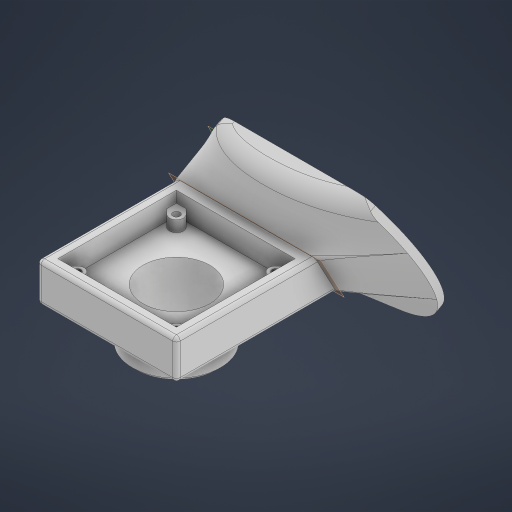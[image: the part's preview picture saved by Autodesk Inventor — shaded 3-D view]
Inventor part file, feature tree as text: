
AUTODESK INVENTOR PART (.ipt)
format: ipt  version: 2023 (Build 270158000, 158)  size: 585,216 bytes
history: native  units: in
note: dims shown in document units (in); Inventor stores cm internally (conversion verified against a paired STEP export)
features: sketch x10, extrude x7, hole x3, fillet x3, plane x2, chamfer x2, other x2, projected_geometry x2, loft x1
ambient origin geometry x8: Origin, YZ Plane, XZ Plane, XY Plane, X Axis, Y Axis, Z Axis, Center Point
bodies: Solid1 (feature_tree)
feature tree (32):
  extrude  "Extrusion1"  Depth=0.525in
  extrude  "Extrusion2"  Depth=0.4252in
  plane  "Work Plane1"
  extrude  "Extrusion3"  Depth=0.6in
  loft  "Loft1"
  extrude  "Extrusion4"  TaperAngle=0.0deg  [1 undecoded]
  hole  "Hole1"  [1 undecoded]
  extrude  "Extrusion5"  Depth=1.1875in
  extrude  "Extrusion6"  Depth=0.1839in
  hole  "Hole2"  [1 undecoded]
  plane  "Work Plane2"
  hole  "Hole3"  [1 undecoded]
  fillet  "Fillet1"  Radius=0.9792in
  chamfer  "Chamfer1"  Angle=45.0deg  [1 undecoded]
  fillet  "Fillet2"  Radius=0.3in
  extrude  "Extrusion7"  Depth=0.15in
  fillet  "Fillet3"  Radius=0.05in
  chamfer  "Chamfer2"  Distance=0.05in Angle=45.0deg
  sketch  "Sketch1"  dims[d0=1.875in d1=0.525in]
  sketch  "Sketch2"  dims[d2=1.875in d3=0.0in d4=0.4252in]
  sketch  "Sketch3"  dims[d5=1.875in d6=0.0in d7=0.6in]
  other  "Edges1"
  other  "Edges2"
  sketch  "Sketch4"  dims[d9=2.75in d10=0.1in d11=0.0in]
  projected_geometry  "Projected Loop1"
  sketch  "Sketch5"  dims[d12=0.0in d13=90.0deg d14=0.0in d15=90.0deg]
  sketch  "Sketch6"  dims[d16=1.6in d17=0.3in d18=0.0in]
  sketch  "Sketch7"  dims[d19=0.9in d20=0.75in d21=0.119in d22=0.25in d23=0.6871in d24=1.0in d25=0.8108in d26=1.1875in]
  projected_geometry  "Projected Loop2"
  sketch  "Sketch8"  dims[d27=0.5in d28=0.0in d29=0.1839in]
  sketch  "Sketch9"  dims[d30=1.3386in d31=0.15in d32=0.0in]
  sketch  "Sketch10"  dims[d33=0.094in d34=0.75in d35=0.251in d36=0.15in d37=0.6871in d38=1.0in d39=0.8108in d40=0.9792in d41=0.9792in d42=45.0deg d43=0.3in d44=0.2in d45=0.177in d46=0.75in d47=0.313in d48=0.45in d49=0.5635in d50=1.0in d51=0.8108in d52=0.05in d53=0.05in d54=0.125in d55=45.0deg d56=0.0625in d57=1.0in d58=1.0in d59=0.0in d60=0.25in d61=0.0312in d62=0.125in d63=45.0deg]
note: 5 required parameter values undecoded (feature->parameter linkage not recoverable at this tier; creation-order binding heuristic only, values carry confidence <= 0.55)
